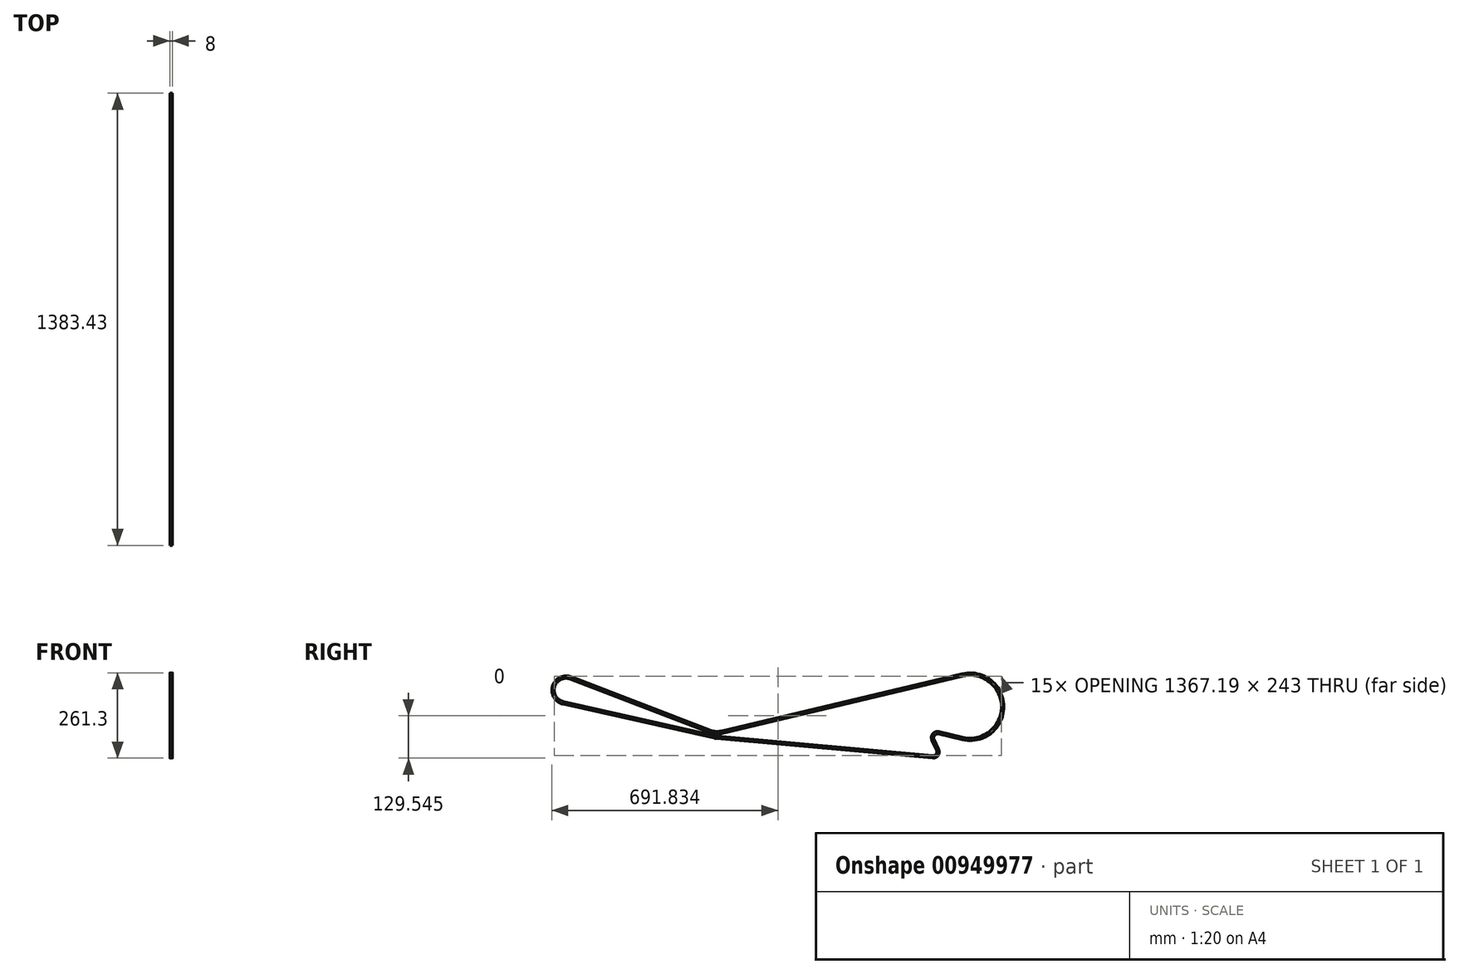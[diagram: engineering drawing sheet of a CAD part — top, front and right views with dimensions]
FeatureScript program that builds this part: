
annotation { "Feature Type Name" : "Feature", "Feature Type Description" : "" }
export const myFeature = defineFeature(function(context is Context, id is Id, definition is map)
    precondition{}
    {
        {
            var Q0;
            Q0=qCreatedBy(makeId("Right.planeOp"),FACE);
            var sketch = newSketch(context, id + "F0", { "sketchPlane" : qUnion([Q0])});
            skArc(sketch, "E0", {"start": v(-22.8, -97.37) * mm, "mid": v(100, 0.16) * mm, "end": v(-23.12, 97.3) * mm});
            skArc(sketch, "E1", {"start": v(-1221.42, 88.02) * mm, "mid": v(-1274.04, 62.27) * mm, "end": v(-1244.55, 11.65) * mm});
            skPoint(sketch, "E2", {"position": v(-1221.42, 88.02) * mm});
            skPoint(sketch, "E3", {"position": v(-1244.55, 11.65) * mm});
            skPoint(sketch, "E4", {"position": v(-44.44, -89.58) * mm});
            skPoint(sketch, "E5", {"position": v(-23.12, 97.3) * mm});
            skLineSegment(sketch, "E6", {"start": v(-1221.42, 88.02) * mm, "end": v(-795.47, -75.47) * mm});
            skLineSegment(sketch, "E7", {"start": v(-760.1, -77.83) * mm, "end": v(-23.12, 97.3) * mm});
            skPoint(sketch, "E8.visualSharp", {"position": v(-778.15, -82.12) * mm});
            skArc(sketch, "E8.filletArc", {"start": v(-795.47, -75.47) * mm, "mid": v(-777.96, -79.33) * mm, "end": v(-760.1, -77.83) * mm});
            skLineSegment(sketch, "E9", {"start": v(-1244.55, 11.65) * mm, "end": v(-780.83, -92.9) * mm});
            skPoint(sketch, "E10.end.orphan", {"position": v(-1503.86, 0) * mm});
            skPoint(sketch, "E11.visualSharp", {"position": v(-745.3, -100.9) * mm});
            skArc(sketch, "E11.filletArc", {"start": v(-780.83, -92.9) * mm, "mid": v(-777.6, -93.51) * mm, "end": v(-774.33, -93.91) * mm});
            skLineSegment(sketch, "E12", {"start": v(-22.8, -97.37) * mm, "end": v(-96.07, -80.2) * mm});
            skLineSegment(sketch, "E13", {"start": v(-113.15, -101) * mm, "end": v(-98.9, -132.42) * mm});
            skLineSegment(sketch, "E14", {"start": v(-113.9, -153.56) * mm, "end": v(-774.33, -93.91) * mm});
            skPoint(sketch, "E15.visualSharp", {"position": v(-125.74, -73.26) * mm});
            skArc(sketch, "E15.filletArc", {"start": v(-96.07, -80.2) * mm, "mid": v(-111.08, -85.3) * mm, "end": v(-113.15, -101) * mm});
            skPoint(sketch, "E16.visualSharp", {"position": v(-88.26, -155.87) * mm});
            skArc(sketch, "E16.filletArc", {"start": v(-113.9, -153.56) * mm, "mid": v(-100.33, -147.3) * mm, "end": v(-98.9, -132.42) * mm});
            skSolve(sketch);
        }
        {
            var Q0;
            Q0=qCreatedBy(makeId("Front.planeOp"),FACE);
            var sketch = newSketch(context, id + "F1", { "sketchPlane" : qUnion([Q0])});
            skLineSegment(sketch, "E17.bottom", {"start": v(4, 103.84) * mm, "end": v(-4, 103.84) * mm});
            skLineSegment(sketch, "E17.top", {"start": v(4, 95.84) * mm, "end": v(-4, 95.84) * mm});
            skLineSegment(sketch, "E17.left", {"start": v(4, 103.84) * mm, "end": v(4, 95.84) * mm});
            skLineSegment(sketch, "E17.right", {"start": v(-4, 103.84) * mm, "end": v(-4, 95.84) * mm});
            skSolve(sketch);
        }
        {
            var Q0;
            Q0=makeQuery(id+"F1.imprint","IMPRINT",FACE,{"disambiguationData":[TD([[makeQuery(id+"F1.imprint","IMPRINT",EDGE,{"derivedFrom":sQuery(id+"F1.wireOp",EDGE,"E17.bottom")}),1.0]])]});
            var Q1;
            Q1=sQuery(id+"F0.wireOp",EDGE,"DYxrVKFV-vadH-UqdX-DBqA-PYYu1d76WIB8");
            var Q2;
            Q2=sQuery(id+"F0.wireOp",EDGE,"E0");
            var Q3;
            Q3=sQuery(id+"F0.wireOp",EDGE,"xD74B9uP-QXV6-qiwC-RsyW-5U2eyFzenrgA");
            var Q4;
            Q4=sQuery(id+"F0.wireOp",EDGE,"E1");
            var Q5;
            Q5=sQuery(id+"F0.wireOp",EDGE,"E10");
            var Q6;
            Q6=sQuery(id+"F0.wireOp",EDGE,"0XPhRpd8-1Edo-j0Qu-TUlV-6sdj9q7OoJMG");
            var Q7;
            Q7=sQuery(id+"F0.wireOp",EDGE,"bQMHr8NS-wXjP-zFau-vBJu-ZDXgYdk95Q02");
            var Q8;
            Q8=sQuery(id+"F0.wireOp",EDGE,"vgkyxV5n-bpPJ-8GUQ-9d85-pQl3E2cZ3X9a");
            var Q9;
            Q9=sQuery(id+"F0.wireOp",EDGE,"tFtKp8hJ-km3c-7Cv2-0KuD-iI712tNKkXFV");
            var Q10;
            Q10=sQuery(id+"F0.wireOp",EDGE,"E6");
            var Q11;
            Q11=sQuery(id+"F0.wireOp",EDGE,"E7");
            var Q12;
            Q12=sQuery(id+"F0.wireOp",EDGE,"E8.filletArc");
            var Q13;
            Q13=sQuery(id+"F0.wireOp",EDGE,"J9ly9QLt-bY3f-255L-cukv-xCgjAtlNKodL");
            var Q14;
            Q14=sQuery(id+"F0.wireOp",EDGE,"E11.filletArc");
            var Q15;
            Q15=sQuery(id+"F0.wireOp",EDGE,"E9");
            var Q16;
            Q16=sQuery(id+"F0.wireOp",EDGE,"E14");
            var Q17;
            Q17=sQuery(id+"F0.wireOp",EDGE,"E16.filletArc");
            var Q18;
            Q18=sQuery(id+"F0.wireOp",EDGE,"E13");
            var Q19;
            Q19=sQuery(id+"F0.wireOp",EDGE,"E15.filletArc");
            var Q20;
            Q20=sQuery(id+"F0.wireOp",EDGE,"E12");
            sweep(context, id + "F2", {"profiles" : qUnion([Q0]), "path" : qUnion([Q1, Q2, Q3, Q4, Q5, Q6, Q7, Q8, Q9, Q10, Q11, Q12, Q13, Q14, Q15, Q16, Q17, Q18, Q19, Q20])});
        }
    });
